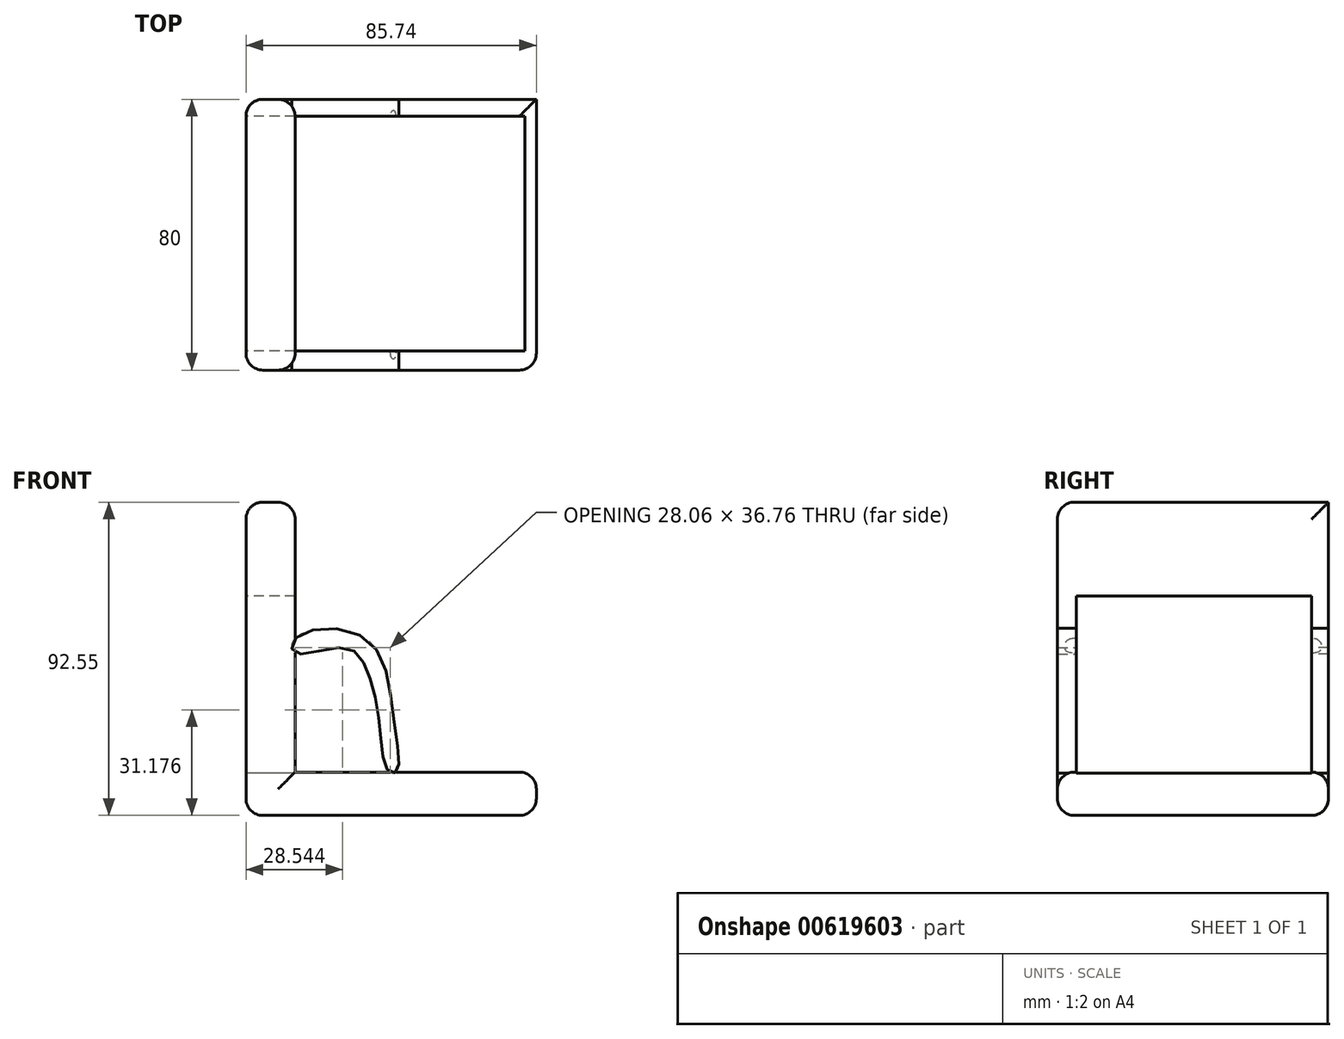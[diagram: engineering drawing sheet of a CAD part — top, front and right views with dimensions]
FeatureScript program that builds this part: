
annotation { "Feature Type Name" : "Feature", "Feature Type Description" : "" }
export const myFeature = defineFeature(function(context is Context, id is Id, definition is map)
    precondition{}
    {
        {
            var Q0;
            Q0=qCreatedBy(makeId("Front.planeOp"),FACE);
            var sketch = newSketch(context, id + "F0", { "sketchPlane" : qUnion([Q0])});
            skLineSegment(sketch, "E0", {"start": v(-52.99, 49.74) * mm, "end": v(-52.99, -42.87) * mm});
            skLineSegment(sketch, "E1", {"start": v(-52.99, -42.87) * mm, "end": v(32.75, -42.87) * mm});
            skLineSegment(sketch, "E2", {"start": v(32.75, -42.87) * mm, "end": v(32.75, -30.08) * mm});
            skLineSegment(sketch, "E3", {"start": v(32.75, -30.08) * mm, "end": v(-38.48, -30.08) * mm});
            skLineSegment(sketch, "E4", {"start": v(-38.48, -30.08) * mm, "end": v(-38.48, 49.55) * mm});
            skLineSegment(sketch, "E5", {"start": v(-38.48, 49.55) * mm, "end": v(-52.99, 49.74) * mm});
            skSolve(sketch);
        }
        {
            var Q0;
            Q0=makeQuery(id+"F0.imprint","IMPRINT",FACE,{"disambiguationData":[TD([[makeQuery(id+"F0.imprint","IMPRINT",EDGE,{"derivedFrom":sQuery(id+"F0.wireOp",EDGE,"E0")}),1.0]])]});
            extrude(context, id + "F1", {"entities" : qUnion([Q0]), "depth" : 80 * mm, "offsetDistance" : 25 * mm});
        }
        {
            var Q0;
            Q0=makeQuery(id+"F1.opExtrude","CAP_EDGE",EDGE,{"disambiguationData":[OSD([sQuery(id+"F0.wireOp",EDGE,"E5")])],"isStart":false});
            var Q1;
            Q1=makeQuery(id+"F1.opExtrude","CAP_EDGE",EDGE,{"disambiguationData":[OSD([sQuery(id+"F0.wireOp",EDGE,"E0")])],"isStart":false});
            var Q2;
            Q2=makeQuery(id+"F1.opExtrude","CAP_EDGE",EDGE,{"disambiguationData":[OSD([sQuery(id+"F0.wireOp",EDGE,"E4")])],"isStart":false});
            var Q3;
            Q3=makeQuery(id+"F1.opExtrude","CAP_FACE",FACE,{"disambiguationData":[OSD([sQuery(id+"F0.wireOp",EDGE,"E0"),sQuery(id+"F0.wireOp",EDGE,"E1"),sQuery(id+"F0.wireOp",EDGE,"E2"),sQuery(id+"F0.wireOp",EDGE,"E3"),sQuery(id+"F0.wireOp",EDGE,"E4"),sQuery(id+"F0.wireOp",EDGE,"E5")])],"isStart":false});
            var Q4;
            Q4=makeQuery(id+"F1.opExtrude","SWEPT_EDGE",EDGE,{"disambiguationData":[OSD([sQuery(id+"F0.wireOp",EDGE,"E4"),sQuery(id+"F0.wireOp",EDGE,"E5")])]});
            var Q5;
            Q5=makeQuery(id+"F1.opExtrude","SWEPT_EDGE",EDGE,{"disambiguationData":[OSD([sQuery(id+"F0.wireOp",EDGE,"E2"),sQuery(id+"F0.wireOp",EDGE,"E3")])]});
            var Q6;
            Q6=makeQuery(id+"F1.opExtrude","SWEPT_EDGE",EDGE,{"disambiguationData":[OSD([sQuery(id+"F0.wireOp",EDGE,"E1"),sQuery(id+"F0.wireOp",EDGE,"E2")])]});
            var Q7;
            Q7=makeQuery(id+"F1.opExtrude","CAP_EDGE",EDGE,{"disambiguationData":[OSD([sQuery(id+"F0.wireOp",EDGE,"E3")])],"isStart":true});
            var Q8;
            Q8=makeQuery(id+"F1.opExtrude","CAP_EDGE",EDGE,{"disambiguationData":[OSD([sQuery(id+"F0.wireOp",EDGE,"E4")])],"isStart":true});
            var Q9;
            Q9=makeQuery(id+"F1.opExtrude","CAP_EDGE",EDGE,{"disambiguationData":[OSD([sQuery(id+"F0.wireOp",EDGE,"E0")])],"isStart":true});
            var Q10;
            Q10=makeQuery(id+"F1.opExtrude","CAP_EDGE",EDGE,{"disambiguationData":[OSD([sQuery(id+"F0.wireOp",EDGE,"E1")])],"isStart":true});
            var Q11;
            Q11=makeQuery(id+"F1.opExtrude","SWEPT_EDGE",EDGE,{"disambiguationData":[OSD([sQuery(id+"F0.wireOp",EDGE,"E0"),sQuery(id+"F0.wireOp",EDGE,"E1")])]});
            var Q12;
            Q12=makeQuery(id+"F1.opExtrude","SWEPT_EDGE",EDGE,{"disambiguationData":[OSD([sQuery(id+"F0.wireOp",EDGE,"E0"),sQuery(id+"F0.wireOp",EDGE,"E5")])]});
            fillet(context, id + "F2", {"entities" : qUnion([Q0, Q1, Q2, Q3, Q4, Q5, Q6, Q7, Q8, Q9, Q10, Q11, Q12]), "radius" : 5 * mm, "tangentPropagation" : true, "allowEdgeOverflow" : false});
        }
        {
            var Q0;
            Q0=qCreatedBy(makeId("Front.planeOp"),FACE);
            var sketch = newSketch(context, id + "F3", { "sketchPlane" : qUnion([Q0])});
            skFitSpline(sketch, "E6", {"points": [v(-38.25, 9.68) * mm, v(-17.76, 9.5) * mm, v(-9.3, -14.75) * mm, v(-8.55, -29.98) * mm, v(-11, -29.6) * mm, v(-13.44, -17.39) * mm, v(-17.2, 0) * mm, v(-24.15, 6.67) * mm, v(-38.44, 5.17) * mm, v(-38.25, 9.68) * mm]});
            skSolve(sketch);
        }
        {
            var Q0;
            Q0 = qSketchRegion(id + "F3", true);
            extrude(context, id + "F4", {"entities" : qUnion([Q0]), "operationType" : NewBodyOperationType.ADD, "depth" : 80 * mm, "offsetDistance" : 25 * mm});
        }
        {
            var Q0;
            Q0=qCreatedBy(makeId("Right.planeOp"),FACE);
            var sketch = newSketch(context, id + "F5", { "sketchPlane" : qUnion([Q0])});
            skLineSegment(sketch, "E7.bottom", {"start": v(-74.39, 21.9) * mm, "end": v(-5.04, 21.9) * mm});
            skLineSegment(sketch, "E7.top", {"start": v(-74.39, -30.35) * mm, "end": v(-5.04, -30.35) * mm});
            skLineSegment(sketch, "E7.left", {"start": v(-74.39, 21.9) * mm, "end": v(-74.39, -30.35) * mm});
            skLineSegment(sketch, "E7.right", {"start": v(-5.04, 21.9) * mm, "end": v(-5.04, -30.35) * mm});
            skSolve(sketch);
        }
        {
            var Q0;
            Q0 = qSketchRegion(id + "F5", true);
            extrude(context, id + "F6", {"entities" : qUnion([Q0]), "operationType" : NewBodyOperationType.REMOVE, "endBound" : BoundingType.THROUGH_ALL, "depth" : 25 * mm, "offsetDistance" : 25 * mm, "hasSecondDirection" : true, "secondDirectionOppositeDirection" : true, "secondDirectionDepth" : 80 * mm});
        }
    });
